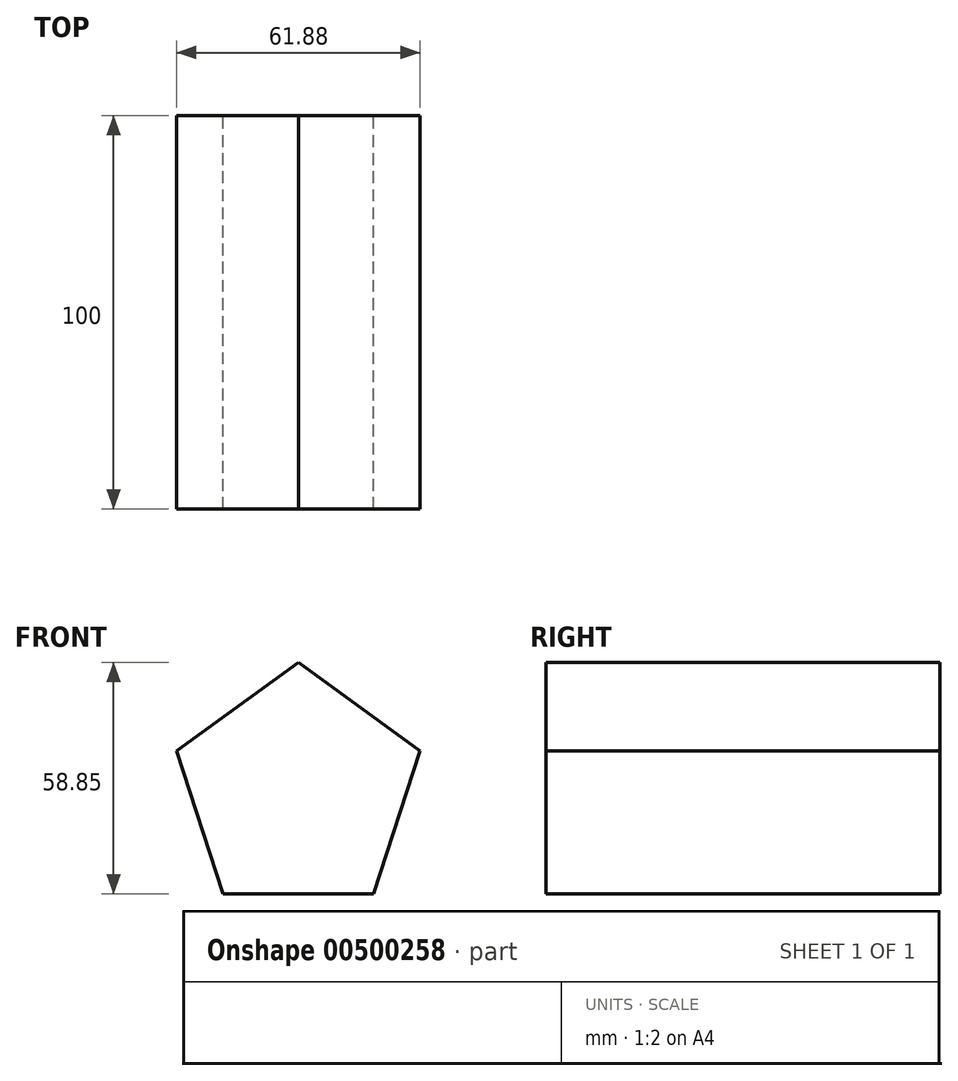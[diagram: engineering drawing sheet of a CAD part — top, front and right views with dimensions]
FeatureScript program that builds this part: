
annotation { "Feature Type Name" : "Feature", "Feature Type Description" : "" }
export const myFeature = defineFeature(function(context is Context, id is Id, definition is map)
    precondition{}
    {
        {
            var Q0;
            Q0=qCreatedBy(makeId("Front.planeOp"),FACE);
            var sketch = newSketch(context, id + "F0", { "sketchPlane" : qUnion([Q0])});
            skCircle(sketch, "E0.cCircle", {"center": v(0, 0) * mm, "radius": 32.53 * mm, "construction": true});
            skLineSegment(sketch, "E0.0", {"start": v(30.94, 10.05) * mm, "end": v(0, 32.53) * mm});
            skLineSegment(sketch, "E0.1", {"start": v(19.12, -26.32) * mm, "end": v(30.94, 10.05) * mm});
            skLineSegment(sketch, "E0.2", {"start": v(-19.12, -26.32) * mm, "end": v(19.12, -26.32) * mm});
            skLineSegment(sketch, "E0.3", {"start": v(-30.94, 10.05) * mm, "end": v(-19.12, -26.32) * mm});
            skLineSegment(sketch, "E0.4", {"start": v(0, 32.53) * mm, "end": v(-30.94, 10.05) * mm});
            skSolve(sketch);
        }
        {
            var Q0;
            Q0=makeQuery(id+"F0.imprint","IMPRINT",FACE,{"disambiguationData":[TD([[makeQuery(id+"F0.imprint","IMPRINT",EDGE,{"derivedFrom":sQuery(id+"F0.wireOp",EDGE,"E0.0")}),1.0]])]});
            extrude(context, id + "F1", {"entities" : qUnion([Q0]), "depth" : 100 * mm});
        }
    });
